# Revit family: LEGRAND_ECLAIRAGE_DE_SECURITE_SATI_ADRESSABLE
name_source: partatom
category: Luminaires
units: mm (PartAtom-declared; Revit-internal decimal feet)

## family parameters
Cote de connecteur circulaire = Utiliser le diamètre
Couper avec des vides une fois chargée = Non
Hôte = Face
Partagée = Non
Point de calcul de pièce = Non
Source d'éclairage = Non
Type d'élément = Normal

## types (13) — shared parameters
Accessoire non disponible = Pas d'accessoire ou Non disponible
Alimentation = décentralisé (batterie individuelle)
Classe de protection = II
Condition Générale d'Utilisation = https://export.legrand.com
Elévation par défaut = 1219 mm
Etat des accus = NiMh
Fabricant = LEGRAND
Installation de surveillance = auto-test automatique
Porte_picto = Porte picto Triangulaire Ref 062676
Source lumineuse = LED non interchangeable
Tension nominale (Min-Max V) = 207-253
Type de commutation = mode veille
Type de tension = CA
URL = http://www.legrandoc.com

## per-type parameters (varying)
- Permanent_IP43: Accessoire 1=Pas d'accessoire ou Non disponible; Accessoire 2=Pas d'accessoire ou Non disponible; Accessoire 3=Pas d'accessoire ou Non disponible; Accessoire 4=Pas d'accessoire ou Non disponible; Autonomie (H)=1; Batterie rechange=061096; Classe de protection (IP)=IP43; Couleur du boitier=blanc; Description=BAES PERMANENT A LEDS ECO2 IP43 IK07 SATI ADRESSABLE 450LM NIMH; Diamètre externe=0 mm  [stored 0 ft]; Flux lumineux en mode d'urgence (lm)=450; Form=IP_43P; Forme alternative=IP_43P; Hauteur-Profondeur=55 mm  [stored 0.180446 ft]; IP 66=Non; Largeur=125 mm  [stored 0.410105 ft]; Largeur de montage=0 mm  [stored 0 ft]; Longeur d'encastrement=0 mm  [stored 0 ft]; Longueur=285 mm  [stored 0.935039 ft]; Matériau du boitier=LEGRAND - Plastique; Modèle=062646; Objet connecté=Non; Picto=Pas de picto; Profondeur d'encastrement=0 mm  [stored 0 ft]; Puissance de la lampe (W)=6; Type de montage=pose murale en saillie
- Amb_IP43: Accessoire 1=Encastrement sans plaque Ref 062694; Accessoire 2=Suspension BAES et LSC Ref 062677; Accessoire 3=Pas d'accessoire ou Non disponible; Accessoire 4=Pas d'accessoire ou Non disponible; Adapté au style de marquage=autre; Autonomie (H)=1; Batterie rechange=061081; Classe de protection (IP)=IP43; Consommation veille (mA)=5.5; Couleur du boitier=blanc; Description=BAES AMBIANCE A LEDS PLASTIQUE IP43  IK07 SATI ADRESSABLE; Diamètre externe=0 mm  [stored 0 ft]; Entre axe fixation horizontale (Min-Max) (mm)=60-95; Entre axe fixation verticale (Min-Max) (mm)=0-65.5; Flux lumineux en mode d'urgence (lm)=400; Form=IP_43-66 : IP_43; Forme alternative=IP_43-66 : IP_43; Fréquence (Hz)=50-60; Hauteur-Profondeur=45 mm  [stored 0.147638 ft]; IP 66=Non; Largeur=125 mm  [stored 0.410105 ft]; Largeur de montage=160 mm  [stored 0.524934 ft]; Longeur d'encastrement=275 mm; Longueur=225 mm  [stored 0.738189 ft]; Matériau du boitier=LEGRAND - Plastique; Modèle=062665; Objet connecté=Oui; Picto=Pas de picto; Profondeur d'encastrement=55 mm  [stored 0.180446 ft]; Puissance de la lampe (W)=4; Resistance aux chocs IK=IK07; Température utilisation (Min-Max °C)=-5-35; Type de borne=borne automatique; Type de montage=montage en saillie-encastrement
- BAEH_IP43: Accessoire 1=Porte picto Vertical Ref 062675; Accessoire 2=Encastrement sans plaque Ref 062694; Accessoire 3=Suspension avec plaque BAES et LSC Ref 062677+062675; Accessoire 4=Suspension BAES et LSC Ref 062677; Adapté au style de marquage=autre; Autonomie (H)=5; Batterie rechange=061080; Classe de protection (IP)=IP43; Consommation veille (mA)=3; Couleur du boitier=blanc; Description=BAEH HABITATION A LEDS PLASTIQUE IP 43 IK07 SATI ADRESSABLE; Diamètre externe=0 mm  [stored 0 ft]; Entre axe fixation horizontale (Min-Max) (mm)=60-95; Entre axe fixation verticale (Min-Max) (mm)=0-65.5; Flux lumineux en mode d'urgence (lm)=8; Form=IP_43-66 : IP_43; Forme alternative=IP_43-66 : IP_43; Fréquence (Hz)=50-60; Hauteur-Profondeur=45 mm  [stored 0.147638 ft]; IP 66=Non; Largeur=125 mm  [stored 0.410105 ft]; Largeur de montage=160 mm  [stored 0.524934 ft]; Longeur d'encastrement=275 mm; Longueur=225 mm  [stored 0.738189 ft]; Matériau du boitier=LEGRAND - Plastique; Modèle=062650; Objet connecté=Oui; Picto=Pas de picto; Profondeur d'encastrement=55 mm  [stored 0.180446 ft]; Puissance de la lampe (W)=0.5; Resistance aux chocs IK=IK07; Température utilisation (Min-Max °C)=-5-35; Type de borne=borne automatique; Type de montage=montage en saillie-encastrement
- BAES+BAEH_IP43: Accessoire 1=Porte picto Vertical Ref 062675; Accessoire 2=Encastrement sans plaque Ref 062694; Accessoire 3=Suspension avec plaque BAES et LSC Ref 062677+062675; Accessoire 4=Suspension BAES et LSC Ref 062677; Adapté au style de marquage=feuillet-plaque inséré(e); Autonomie (H)=1; Batterie rechange=2 x 061080; Classe de protection (IP)=IP43; Consommation veille (mA)=4; Couleur du boitier=blanc; Description=BAES+BAEH EVACUATION A LEDS PLASTIQUE IP43 IK07 SATI ADRESSABLE; Diamètre externe=0 mm  [stored 0 ft]; Entre axe fixation horizontale (Min-Max) (mm)=60-95; Entre axe fixation verticale (Min-Max) (mm)=0-65.5; Flux lumineux en mode d'urgence (lm)=45; Form=IP_43-66 : IP_43; Forme alternative=IP_43-66 : IP_43; Fréquence (Hz)=50-60; Hauteur-Profondeur=45 mm  [stored 0.147638 ft]; IP 66=Non; Largeur=125 mm  [stored 0.410105 ft]; Largeur de montage=160 mm  [stored 0.524934 ft]; Longeur d'encastrement=275 mm; Longueur=225 mm  [stored 0.738189 ft]; Matériau du boitier=LEGRAND - Plastique; Modèle=062660; Objet connecté=Oui; Picto=Picto Evac; Profondeur d'encastrement=55 mm  [stored 0.180446 ft]; Puissance de la lampe (W)=1; Resistance aux chocs IK=IK07; Température utilisation (Min-Max °C)=-5-35; Type de borne=borne automatique; Type de montage=montage en saillie-encastrement
- DBR_IP43: Accessoire 1=Porte picto Vertical Ref 062675; Accessoire 2=Encastrement sans plaque Ref 062694; Accessoire 3=Suspension BAES et LSC Ref 062677; Accessoire 4=Suspension avec plaque BAES et LSC Ref 062677+062675; Adapté au style de marquage=feuillet-plaque inséré(e); Autonomie (H)=1; Batterie rechange=2 x 061080; Classe de protection (IP)=IP43; Consommation veille (mA)=3; Couleur du boitier=blanc; Description=BAES EVACUATION AVEC DISPOSITIF DE BALISAGE RENFORCE A LEDS IP43 SATI ADR; Diamètre externe=0 mm  [stored 0 ft]; Entre axe fixation horizontale (Min-Max) (mm)=60-95; Entre axe fixation verticale (Min-Max) (mm)=0-65.5; Flux lumineux en mode d'urgence (lm)=45; Form=IP_43-66 : IP_43; Forme alternative=IP_43-66 : IP_43; Fréquence (Hz)=50-60; Hauteur-Profondeur=45 mm  [stored 0.147638 ft]; IP 66=Non; Largeur=125 mm  [stored 0.410105 ft]; Largeur de montage=160 mm  [stored 0.524934 ft]; Longeur d'encastrement=275 mm; Longueur=225 mm  [stored 0.738189 ft]; Matériau du boitier=LEGRAND - Plastique; Modèle=062634; Objet connecté=Oui; Picto=Picto Rassemblement; Profondeur d'encastrement=55 mm  [stored 0.180446 ft]; Puissance de la lampe (W)=1; Resistance aux chocs IK=IK07; Température utilisation (Min-Max °C)=-5-35; Type de borne=borne automatique; Type de montage=montage en saillie-encastrement
- Evac_IP43: Accessoire 1=Porte picto Vertical Ref 062675; Accessoire 2=Encastrement sans plaque Ref 062694; Accessoire 3=Suspension BAES et LSC Ref 062677; Accessoire 4=Suspension avec plaque BAES et LSC Ref 062677+062675; Adapté au style de marquage=feuillet-plaque inséré(e); Autonomie (H)=1; Batterie rechange=061080; Classe de protection (IP)=IP43; Consommation veille (mA)=3; Couleur du boitier=blanc; Description=BAES EVACUATION A LEDS PLASTIQUE IP 43 IK07 SATI ADRESSABLE; Diamètre externe=0 mm  [stored 0 ft]; Entre axe fixation horizontale (Min-Max) (mm)=60-95; Entre axe fixation verticale (Min-Max) (mm)=0-65.5; Flux lumineux en mode d'urgence (lm)=45; Form=IP_43-66 : IP_43; Forme alternative=IP_43-66 : IP_43; Fréquence (Hz)=50-60; Hauteur-Profondeur=45 mm  [stored 0.147638 ft]; IP 66=Non; Largeur=125 mm  [stored 0.410105 ft]; Largeur de montage=160 mm  [stored 0.524934 ft]; Longeur d'encastrement=275 mm; Longueur=225 mm  [stored 0.738189 ft]; Matériau du boitier=LEGRAND - Plastique; Modèle=062625; Objet connecté=Oui; Picto=Picto Evac; Profondeur d'encastrement=55 mm  [stored 0.180446 ft]; Puissance de la lampe (W)=0.5; Resistance aux chocs IK=IK07; Température utilisation (Min-Max °C)=-5-35; Type de borne=borne automatique; Type de montage=montage en saillie-encastrement
- Amb_IP66: Accessoire 1=Pas d'accessoire ou Non disponible; Accessoire 2=Pas d'accessoire ou Non disponible; Accessoire 3=Pas d'accessoire ou Non disponible; Accessoire 4=Pas d'accessoire ou Non disponible; Adapté au style de marquage=autre; Autonomie (H)=1; Batterie rechange=061081; Classe de protection (IP)=IP66; Consommation veille (mA)=5.5; Couleur du boitier=blanc; Description=BAES AMBIANCE A LEDS PLASTIQUE IP66  IK10 SATI ADRESSABLE; Diamètre externe=0 mm  [stored 0 ft]; Entre axe fixation horizontale (Min-Max) (mm)=80-153; Entre axe fixation verticale (Min-Max) (mm)=0-83; Flux lumineux en mode d'urgence (lm)=400; Form=IP_43-66 : IP_66; Forme alternative=IP_43-66 : IP_66; Fréquence (Hz)=50-60; Hauteur-Profondeur=62 mm  [stored 0.203412 ft]; IP 66=Oui; Largeur=125 mm  [stored 0.410105 ft]; Largeur de montage=0 mm  [stored 0 ft]; Longeur d'encastrement=0 mm  [stored 0 ft]; Longueur=225 mm  [stored 0.738189 ft]; Matériau du boitier=LEGRAND - Plastique; Modèle=062666; Objet connecté=Oui; Picto=Pas de picto; Profondeur d'encastrement=0 mm  [stored 0 ft]; Puissance de la lampe (W)=4; Resistance aux chocs IK=IK10; Température utilisation (Min-Max °C)=-5-35; Type de borne=borne automatique; Type de montage=montage en saillie-encastrement
- BAEH_IP66: Accessoire 1=Porte picto Triangulaire Ref 062676; Accessoire 2=Pas d'accessoire ou Non disponible; Accessoire 3=Pas d'accessoire ou Non disponible; Accessoire 4=Pas d'accessoire ou Non disponible; Adapté au style de marquage=autre; Autonomie (H)=5; Batterie rechange=061080; Classe de protection (IP)=IP66; Consommation veille (mA)=3; Couleur du boitier=blanc; Description=BAEH HABITATION A LEDS PLASTIQUE IP 66 IK10 SATI ADRESSABLE; Diamètre externe=0 mm  [stored 0 ft]; Entre axe fixation horizontale (Min-Max) (mm)=80-153; Entre axe fixation verticale (Min-Max) (mm)=0-83; Flux lumineux en mode d'urgence (lm)=8; Form=IP_43-66 : IP_66; Forme alternative=IP_43-66 : IP_43; Fréquence (Hz)=50-60; Hauteur-Profondeur=62 mm  [stored 0.203412 ft]; IP 66=Oui; Largeur=125 mm  [stored 0.410105 ft]; Largeur de montage=0 mm  [stored 0 ft]; Longeur d'encastrement=0 mm  [stored 0 ft]; Longueur=225 mm  [stored 0.738189 ft]; Matériau du boitier=LEGRAND - Plastique; Modèle=062652; Objet connecté=Oui; Picto=Pas de picto; Profondeur d'encastrement=0 mm  [stored 0 ft]; Puissance de la lampe (W)=0.5; Resistance aux chocs IK=IK10; Température utilisation (Min-Max °C)=-5-35; Type de borne=borne automatique; Type de montage=montage en saillie-encastrement
- BAES+BAEH_IP66: Accessoire 1=Porte picto Triangulaire Ref 062676; Accessoire 2=Pas d'accessoire ou Non disponible; Accessoire 3=Pas d'accessoire ou Non disponible; Accessoire 4=Pas d'accessoire ou Non disponible; Adapté au style de marquage=feuillet-plaque inséré(e); Autonomie (H)=1; Batterie rechange=2 x 061080; Classe de protection (IP)=IP66; Consommation veille (mA)=4; Couleur du boitier=blanc; Description=BAES+BAEH EVACUATION A LEDS PLASTIQUE IP66 IK10 SATI ADRESSABLE; Diamètre externe=0 mm  [stored 0 ft]; Entre axe fixation horizontale (Min-Max) (mm)=80-153; Entre axe fixation verticale (Min-Max) (mm)=0-83; Flux lumineux en mode d'urgence (lm)=45; Form=IP_43-66 : IP_66; Forme alternative=IP_43-66 : IP_43; Fréquence (Hz)=50-60; Hauteur-Profondeur=62 mm  [stored 0.203412 ft]; IP 66=Oui; Largeur=125 mm  [stored 0.410105 ft]; Largeur de montage=0 mm  [stored 0 ft]; Longeur d'encastrement=0 mm  [stored 0 ft]; Longueur=225 mm  [stored 0.738189 ft]; Matériau du boitier=LEGRAND - Plastique; Modèle=062661; Objet connecté=Oui; Picto=Picto Evac; Profondeur d'encastrement=0 mm  [stored 0 ft]; Puissance de la lampe (W)=1; Resistance aux chocs IK=IK10; Température utilisation (Min-Max °C)=-5-35; Type de borne=borne automatique; Type de montage=montage en saillie-encastrement
- DBR_IP66: Accessoire 1=Porte picto Triangulaire Ref 062676; Accessoire 2=Pas d'accessoire ou Non disponible; Accessoire 3=Pas d'accessoire ou Non disponible; Accessoire 4=Pas d'accessoire ou Non disponible; Adapté au style de marquage=feuillet-plaque inséré(e); Autonomie (H)=1; Batterie rechange=2 x 061080; Classe de protection (IP)=IP66; Consommation veille (mA)=3; Couleur du boitier=blanc; Description=BAES EVACUATION AVEC DISPOSITIF DE BALISAGE RENFORCE A LEDS IP66 SATI ADR; Diamètre externe=0 mm  [stored 0 ft]; Entre axe fixation horizontale (Min-Max) (mm)=80-153; Entre axe fixation verticale (Min-Max) (mm)=0-83; Flux lumineux en mode d'urgence (lm)=45; Form=IP_43-66 : IP_66; Forme alternative=IP_43-66 : IP_43; Fréquence (Hz)=50-60; Hauteur-Profondeur=62 mm  [stored 0.203412 ft]; IP 66=Oui; Largeur=125 mm  [stored 0.410105 ft]; Largeur de montage=0 mm  [stored 0 ft]; Longeur d'encastrement=0 mm  [stored 0 ft]; Longueur=225 mm  [stored 0.738189 ft]; Matériau du boitier=LEGRAND - Plastique; Modèle=062636; Objet connecté=Oui; Picto=Picto Rassemblement; Profondeur d'encastrement=0 mm  [stored 0 ft]; Puissance de la lampe (W)=1; Resistance aux chocs IK=IK10; Température utilisation (Min-Max °C)=-5-35; Type de borne=borne automatique; Type de montage=montage en saillie-encastrement
- Evac_IP66: Accessoire 1=Porte picto Triangulaire Ref 062676; Accessoire 2=Pas d'accessoire ou Non disponible; Accessoire 3=Pas d'accessoire ou Non disponible; Accessoire 4=Pas d'accessoire ou Non disponible; Adapté au style de marquage=feuillet-plaque inséré(e); Autonomie (H)=1; Batterie rechange=061080; Classe de protection (IP)=IP66; Consommation veille (mA)=3; Couleur du boitier=blanc; Description=BAES EVACUATION A LEDS PLASTIQUE IP 66 IK10 SATI ADRESSABLE; Diamètre externe=0 mm  [stored 0 ft]; Entre axe fixation horizontale (Min-Max) (mm)=80-153; Entre axe fixation verticale (Min-Max) (mm)=0-83; Flux lumineux en mode d'urgence (lm)=45; Form=IP_43-66 : IP_66; Forme alternative=IP_43-66 : IP_43; Fréquence (Hz)=50-60; Hauteur-Profondeur=62 mm  [stored 0.203412 ft]; IP 66=Oui; Largeur=125 mm  [stored 0.410105 ft]; Largeur de montage=0 mm  [stored 0 ft]; Longeur d'encastrement=0 mm  [stored 0 ft]; Longueur=225 mm  [stored 0.738189 ft]; Matériau du boitier=LEGRAND - Plastique; Modèle=062626; Objet connecté=Oui; Picto=Picto Evac; Profondeur d'encastrement=0 mm  [stored 0 ft]; Puissance de la lampe (W)=0.5; Resistance aux chocs IK=IK10; Température utilisation (Min-Max °C)=-5-35; Type de borne=borne automatique; Type de montage=montage en saillie-encastrement
- Amb_IP67: Accessoire 1=Pas d'accessoire ou Non disponible; Accessoire 2=Pas d'accessoire ou Non disponible; Accessoire 3=Pas d'accessoire ou Non disponible; Accessoire 4=Pas d'accessoire ou Non disponible; Adapté au style de marquage=autre; Autonomie (H)=1; Batterie rechange=061081; Classe de protection (IP)=IP67; Consommation veille (mA)=5.5; Couleur du boitier=acier inoxydable; Description=BAES AMBIANCE A LEDS PLASTIQUE-INOX  IP67 IK07 SATI ADRESSABLE; Diamètre externe=150 mm; Entre axe fixation horizontale (Min-Max) (mm)=30-270; Entre axe fixation verticale (Min-Max) (mm)=0-0; Flux lumineux en mode d'urgence (lm)=400; Form=IP_67; Forme alternative=IP_67; Fréquence (Hz)=50-60; Hauteur-Profondeur=0 mm  [stored 0 ft]; IP 66=Non; Largeur=0 mm  [stored 0 ft]; Largeur de montage=0 mm  [stored 0 ft]; Longeur d'encastrement=0 mm  [stored 0 ft]; Longueur=363 mm  [stored 1.19094 ft]; Matériau du boitier=LEGRAND - Acier inoxydable; Modèle=062669; Objet connecté=Oui; Picto=Pas de picto; Profondeur d'encastrement=0 mm  [stored 0 ft]; Puissance de la lampe (W)=4; Resistance aux chocs IK=IK07; Température utilisation (Min-Max °C)=-5-35; Type de borne=borne à vis; Type de montage=pose murale en saillie
- Evac_IP67: Accessoire 1=Pas d'accessoire ou Non disponible; Accessoire 2=Pas d'accessoire ou Non disponible; Accessoire 3=Pas d'accessoire ou Non disponible; Accessoire 4=Pas d'accessoire ou Non disponible; Adapté au style de marquage=feuillet-plaque inséré(e); Autonomie (H)=1; Batterie rechange=061080; Classe de protection (IP)=IP67; Consommation veille (mA)=3; Couleur du boitier=acier inoxydable; Description=BAES EVACUATION A LEDS PLASTIQUE-INOX IP67 SATI ADRESSABLE; Diamètre externe=150 mm; Entre axe fixation horizontale (Min-Max) (mm)=30-270; Entre axe fixation verticale (Min-Max) (mm)=0-0; Flux lumineux en mode d'urgence (lm)=45; Form=IP_67; Forme alternative=IP_67; Fréquence (Hz)=50-60; Hauteur-Profondeur=0 mm  [stored 0 ft]; IP 66=Non; Largeur=0 mm  [stored 0 ft]; Largeur de montage=0 mm  [stored 0 ft]; Longeur d'encastrement=0 mm  [stored 0 ft]; Longueur=363 mm  [stored 1.19094 ft]; Matériau du boitier=LEGRAND - Acier inoxydable; Modèle=062629; Objet connecté=Oui; Picto=Picto Evac; Profondeur d'encastrement=0 mm  [stored 0 ft]; Puissance de la lampe (W)=0.5; Resistance aux chocs IK=IK07; Température utilisation (Min-Max °C)=-5-35; Type de borne=borne à vis; Type de montage=pose murale en saillie

note: [stored X ft] marks values corroborated as IEEE doubles in the binary element streams (Revit-internal decimal feet)
